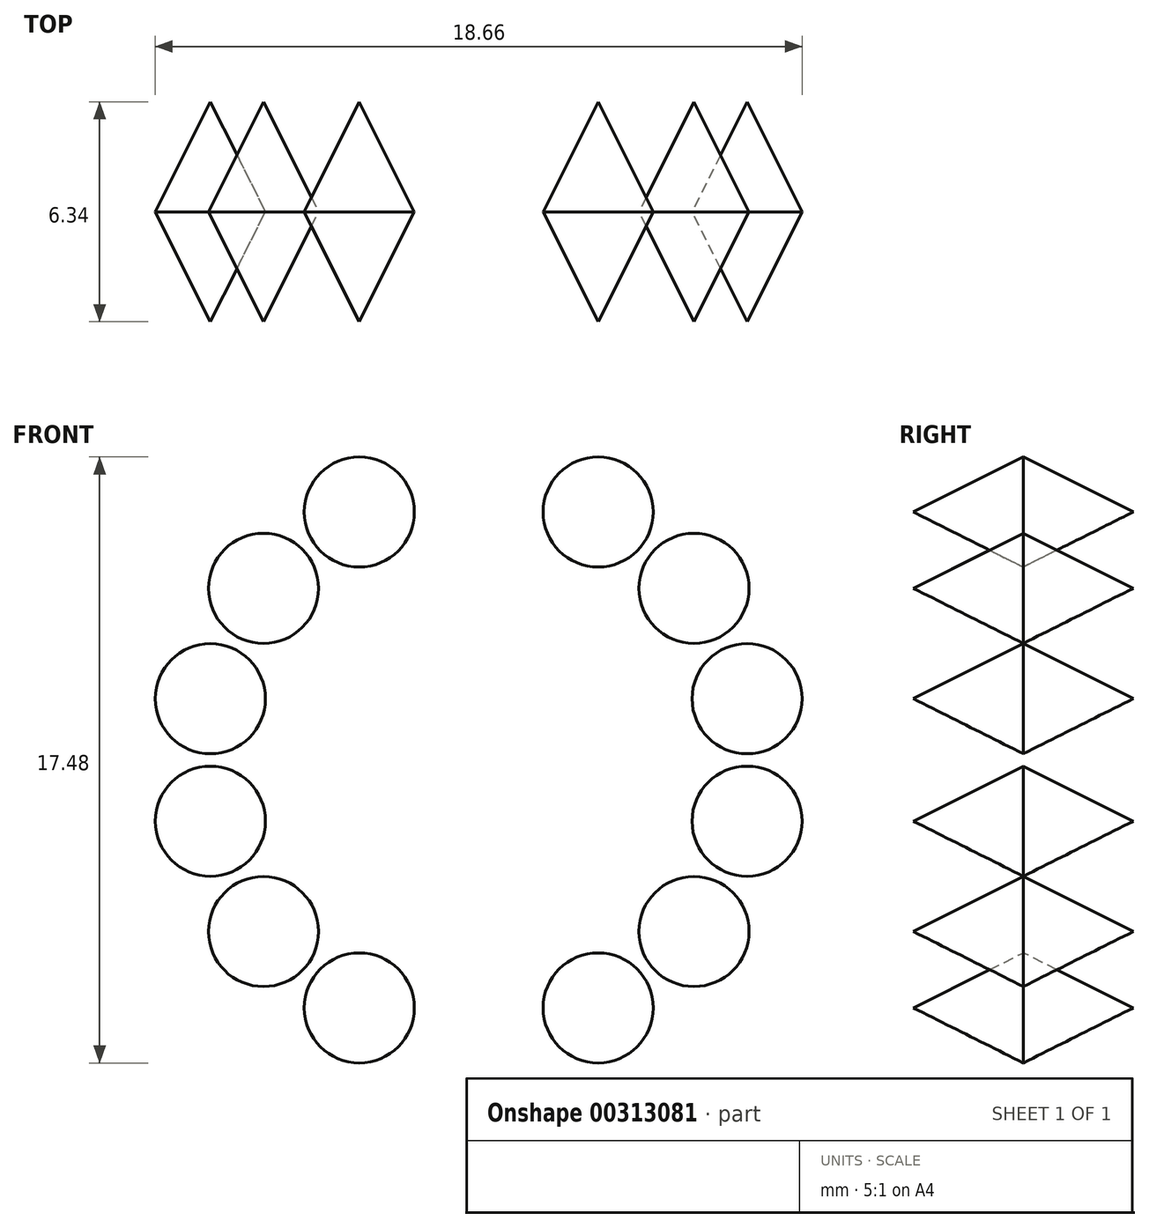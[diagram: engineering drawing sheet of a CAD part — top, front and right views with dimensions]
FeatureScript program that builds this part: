
annotation { "Feature Type Name" : "Feature", "Feature Type Description" : "" }
export const myFeature = defineFeature(function(context is Context, id is Id, definition is map)
    precondition{}
    {
        {
            var Q0;
            Q0=qCreatedBy(makeId("Front.planeOp"),FACE);
            var sketch = newSketch(context, id + "F0", { "sketchPlane" : qUnion([Q0])});
            skCircle(sketch, "E0", {"center": v(0, 7.94) * mm, "radius": 1.59 * mm});
            skCircle(sketch, "E1", {"center": v(0, -7.94) * mm, "radius": 1.59 * mm});
            skCircle(sketch, "E2.1.0", {"center": v(3.44, 7.15) * mm, "radius": 1.59 * mm});
            skCircle(sketch, "E2.1.1", {"center": v(-3.44, -7.15) * mm, "radius": 1.59 * mm});
            skCircle(sketch, "E2.2.0", {"center": v(6.2, 4.95) * mm, "radius": 1.59 * mm});
            skCircle(sketch, "E2.2.1", {"center": v(-6.2, -4.95) * mm, "radius": 1.59 * mm});
            skCircle(sketch, "E2.3.0", {"center": v(7.74, 1.77) * mm, "radius": 1.59 * mm});
            skCircle(sketch, "E2.3.1", {"center": v(-7.74, -1.77) * mm, "radius": 1.59 * mm});
            skCircle(sketch, "E2.4.0", {"center": v(7.74, -1.77) * mm, "radius": 1.59 * mm});
            skCircle(sketch, "E2.4.1", {"center": v(-7.74, 1.77) * mm, "radius": 1.59 * mm});
            skCircle(sketch, "E2.5.0", {"center": v(6.2, -4.95) * mm, "radius": 1.59 * mm});
            skCircle(sketch, "E2.5.1", {"center": v(-6.2, 4.95) * mm, "radius": 1.59 * mm});
            skCircle(sketch, "E2.6.0", {"center": v(3.44, -7.15) * mm, "radius": 1.59 * mm});
            skCircle(sketch, "E2.6.1", {"center": v(-3.44, 7.15) * mm, "radius": 1.59 * mm});
            skPoint(sketch, "E2.center", {"position": v(0, 0) * mm});
            skLineSegment(sketch, "E2.anchor1", {"start": v(0, 0) * mm, "end": v(0, 7.94) * mm, "construction": true});
            skLineSegment(sketch, "E2.anchor2", {"start": v(0, 0) * mm, "end": v(0, -7.94) * mm, "construction": true});
            skSolve(sketch);
        }
        {
            var Q0;
            Q0=makeQuery(id+"F0.imprint","IMPRINT",FACE,{"disambiguationData":[TD([[makeQuery(id+"F0.imprint","IMPRINT",EDGE,{"derivedFrom":sQuery(id+"F0.wireOp",EDGE,"E0")}),1.0]])]});
            var Q1;
            Q1=makeQuery(id+"F0.imprint","IMPRINT",FACE,{"disambiguationData":[TD([[makeQuery(id+"F0.imprint","IMPRINT",EDGE,{"derivedFrom":sQuery(id+"F0.wireOp",EDGE,"E2.1.0")}),1.0]])]});
            var Q2;
            Q2=makeQuery(id+"F0.imprint","IMPRINT",FACE,{"disambiguationData":[TD([[makeQuery(id+"F0.imprint","IMPRINT",EDGE,{"derivedFrom":sQuery(id+"F0.wireOp",EDGE,"E2.3.0")}),1.0]])]});
            var Q3;
            Q3=makeQuery(id+"F0.imprint","IMPRINT",FACE,{"disambiguationData":[TD([[makeQuery(id+"F0.imprint","IMPRINT",EDGE,{"derivedFrom":sQuery(id+"F0.wireOp",EDGE,"E2.4.0")}),1.0]])]});
            var Q4;
            Q4=makeQuery(id+"F0.imprint","IMPRINT",FACE,{"disambiguationData":[TD([[makeQuery(id+"F0.imprint","IMPRINT",EDGE,{"derivedFrom":sQuery(id+"F0.wireOp",EDGE,"E2.5.0")}),1.0]])]});
            var Q5;
            Q5=makeQuery(id+"F0.imprint","IMPRINT",FACE,{"disambiguationData":[TD([[makeQuery(id+"F0.imprint","IMPRINT",EDGE,{"derivedFrom":sQuery(id+"F0.wireOp",EDGE,"E2.6.0")}),1.0]])]});
            var Q6;
            Q6=makeQuery(id+"F0.imprint","IMPRINT",FACE,{"disambiguationData":[TD([[makeQuery(id+"F0.imprint","IMPRINT",EDGE,{"derivedFrom":sQuery(id+"F0.wireOp",EDGE,"E1")}),1.0]])]});
            var Q7;
            Q7=makeQuery(id+"F0.imprint","IMPRINT",FACE,{"disambiguationData":[TD([[makeQuery(id+"F0.imprint","IMPRINT",EDGE,{"derivedFrom":sQuery(id+"F0.wireOp",EDGE,"E2.1.1")}),1.0]])]});
            var Q8;
            Q8=makeQuery(id+"F0.imprint","IMPRINT",FACE,{"disambiguationData":[TD([[makeQuery(id+"F0.imprint","IMPRINT",EDGE,{"derivedFrom":sQuery(id+"F0.wireOp",EDGE,"E2.2.1")}),1.0]])]});
            var Q9;
            Q9=makeQuery(id+"F0.imprint","IMPRINT",FACE,{"disambiguationData":[TD([[makeQuery(id+"F0.imprint","IMPRINT",EDGE,{"derivedFrom":sQuery(id+"F0.wireOp",EDGE,"E2.3.1")}),1.0]])]});
            var Q10;
            Q10=makeQuery(id+"F0.imprint","IMPRINT",FACE,{"disambiguationData":[TD([[makeQuery(id+"F0.imprint","IMPRINT",EDGE,{"derivedFrom":sQuery(id+"F0.wireOp",EDGE,"E2.4.1")}),1.0]])]});
            var Q11;
            Q11=makeQuery(id+"F0.imprint","IMPRINT",FACE,{"disambiguationData":[TD([[makeQuery(id+"F0.imprint","IMPRINT",EDGE,{"derivedFrom":sQuery(id+"F0.wireOp",EDGE,"E2.5.1")}),1.0]])]});
            var Q12;
            Q12=makeQuery(id+"F0.imprint","IMPRINT",FACE,{"disambiguationData":[TD([[makeQuery(id+"F0.imprint","IMPRINT",EDGE,{"derivedFrom":sQuery(id+"F0.wireOp",EDGE,"E2.6.1")}),1.0]])]});
            var Q13;
            Q13=makeQuery(id+"F0.imprint","IMPRINT",FACE,{"disambiguationData":[TD([[makeQuery(id+"F0.imprint","IMPRINT",EDGE,{"derivedFrom":sQuery(id+"F0.wireOp",EDGE,"E2.2.0")}),1.0]])]});
            extrude(context, id + "F1", {"entities" : qUnion([Q0, Q1, Q2, Q3, Q4, Q5, Q6, Q7, Q8, Q9, Q10, Q11, Q12, Q13]), "endBound" : BoundingType.SYMMETRIC, "depth" : 6.35 * mm, "hasDraft" : true, "draftAngle" : 26.6 * degree, "draftPullDirection" : true});
        }
    });
